# Revit family: Windows_Roof-Windows_Velux_Cabrio-Roof-Balcony-GDL
name_source: partatom
category: Windows
revit_build: Autodesk Revit 2015 (Build: 20140606_1530(x64)
units: mm (PartAtom-declared; Revit-internal decimal feet)

## types (2) — shared parameters
2d details = http://www.velux.co.uk
AcousticRating = 34
Air permeability Class = 3
Allowed Roof Slope = 35°-53°
Analytic Construction = <None>
Apron Material = Two layers of aluminium
AssemblyPlace = Denmark
BIMobject category = Roof Windows
BIMobject category code = windows-roof
BIMobject main category = Windows
BIMobject main category code = windows
Bottom panel = 920 mm  [stored 3.01837 ft]
Bottom panel open = No
Brand url = http://www.velux.com
Count = 1
Date of publishing = 4/16/2014
Description = http://www.velux.co.uk
Design country = Denmark
Disclaimer = When installing VELUX roof windows the costumer must make sure to meet local applicable building and fire requirements. VELUX shall not be liable for the objects/drawings and the constructional quality of the installation. Please contact VELUX for technical specifications of VELUX roof windows, flashings, installations products and internal/external accessories.
Edition number = 2
Emergency exit = ??
FireExit = Yes
FireRating = E
FrameOffset – External = 47 mm  [stored 0.154199 ft]
Function = Top/bottom hung roof balcony
GlassColour = Clear
Glazing = Glass
HasDrive = No
HasSillExternal = Yes
HasSillInternal = Yes
Height = 2520 mm  [stored 8.26772 ft]
IFC Classification = Window
Installation instructions = http://www.velux.co.uk
IsExternal = Yes
IsLaminated = Yes
IsTempered = Yes
IsWired = No
Light transmittance = 0.7
Manufacturer = VELUX A/S
Manufacturer URL = www.VELUX.com
Manufacturer country = Denmark
Manufacturer name = VELUX
Masterformat 2014 Code = 08 62 00
Masterformat 2014 Description = Unit Skylights
Material External = Aluminium. Color NCS 7500-N
Material Internal = White paint color NCS 0500-N
Material main = Wood
Material secondary = Glass
NBS Reference Code = 59-72
NBS Reference Description = Roof Window Units
Offset from Roof = 169 mm  [stored 0.554462 ft]
Opening Lines = Yes
Operation = Manuel
Operation Mode = Manuel
PerimeterGlazing m = 6.1924
PerimeterWindow m = 7.32
Product Guid = 56c23bf0-48fe-4bbc-8cc7-7120ee43224e
Product SKU = CABRIO-roof-balcony-GDL
Product data url = https://bimobject.com
Product family = Roof terrace
Product group = GDL
Product url = http://www.velux.co.uk
QR code = http://bimobject.com
Roof Slope = 45.00°
Rough Height = 2560 mm  [stored 8.39895 ft]
SmokeStop = No
Sound Insulation db = 34
Square Reveal Length = 113 mm  [stored 0.370735 ft]
Square Reveal Offset = 66 mm  [stored 0.216535 ft]
Technical description = http://www.professional.velux.co.uk
Thermal Resistance (R) = 0.8333333333
ThermalBridge(Installation) W/mK = 0.09
ThermalBridge(glazing) W/mK = 0.53
ThermalTransmittance = 1.2
Top panel = 1600 mm  [stored 5.24934 ft]
Top panel open = No
UNSPSC Code = 301516
URL = www.VELUX.dk
Ultraviolet Transmittance = 0.05
Uniclass 1.4 Code = JL11
Uniclass 1.4 Description = Rooflights/Roof windows
Uniclass 2.0 Code = PR-59-72
Uniclass 2.0 Description = Roof Window Units
Ventilations flap areal mm2 = 5600
Warranty Years = 5 (10 with BDX)
Water Tightness Class = 9A
Within Standard Sizes = Yes
g-value = 0.5
zero-valued in all types: Cost, GlassLayers, GlassThickness1, GlassThickness2, GlassThickness3, Placement Height, ShadingCoefficient, SolarAbsorption, SolarHeatGainTransmittance, SolarReflectance, SolarTransmittance, VisibleLightReflectance, VisibleLightTransmittance

## per-type parameters (varying)
| type | Rough Width | Width |
| GDL size 940x2520 (PK19) | 980 mm  [stored 3.21522 ft] | 940 mm  [stored 3.08399 ft] |
| GDL size 1140x2520 (SK19) | 1180 mm  [stored 3.87139 ft] | 1140 mm  [stored 3.74016 ft] |

note: [stored X ft] marks values corroborated as IEEE doubles in the binary element streams (Revit-internal decimal feet)

## geometry (parser evidence)
native form markers: Blend x24, Sweep x8
no freeform markers — native parametric forms only
